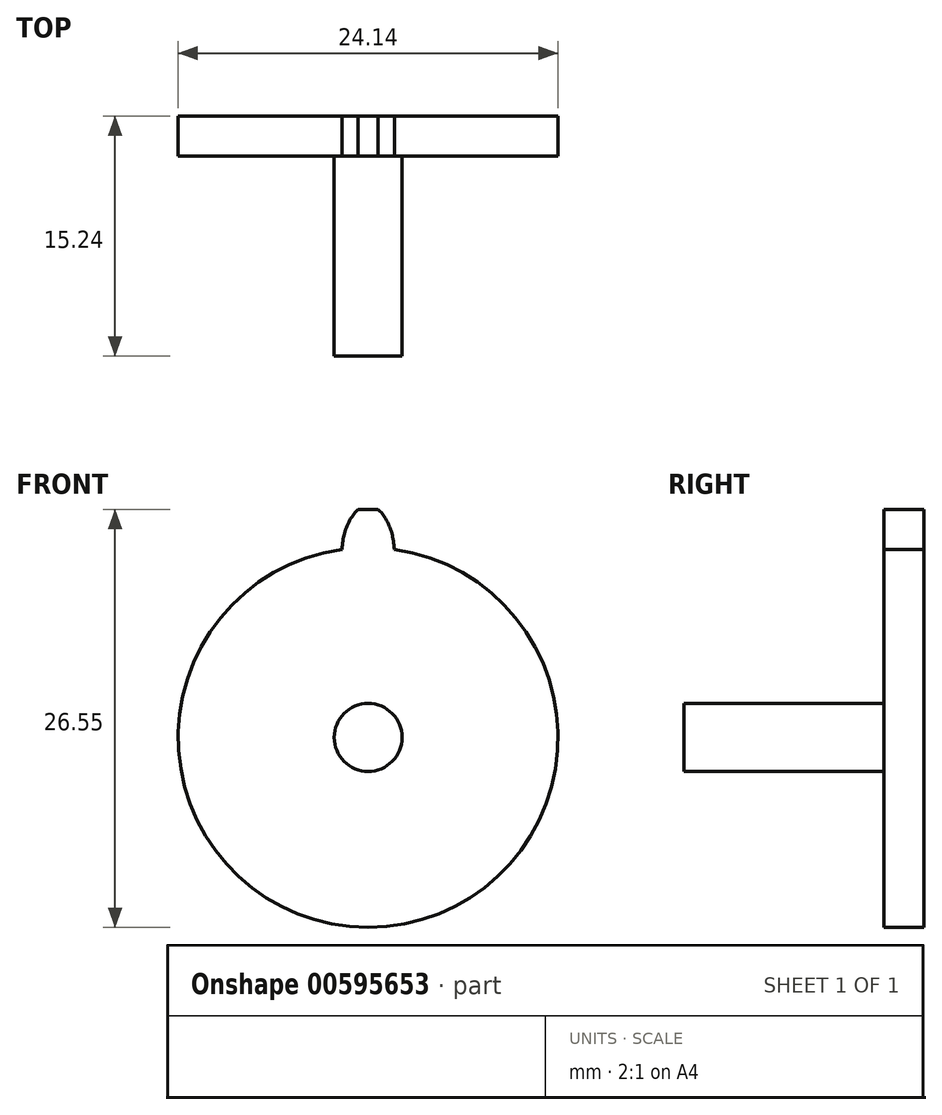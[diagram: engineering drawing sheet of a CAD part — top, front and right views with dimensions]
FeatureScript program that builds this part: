
annotation { "Feature Type Name" : "Feature", "Feature Type Description" : "" }
export const myFeature = defineFeature(function(context is Context, id is Id, definition is map)
    precondition{}
    {
        {
            var Q0;
            Q0=qCreatedBy(makeId("Front.planeOp"),FACE);
            var sketch = newSketch(context, id + "F0", { "sketchPlane" : qUnion([Q0])});
            skCircle(sketch, "E0", {"center": v(0, 0) * mm, "radius": 12.07 * mm});
            skLineSegment(sketch, "E1", {"start": v(-0.64, 14.48) * mm, "end": v(0.64, 14.48) * mm});
            skFitSpline(sketch, "E2", {"points": [v(-1.67, 11.95) * mm, v(-1.33, 13.46) * mm, v(-0.63, 14.48) * mm], "startDerivative": vector(0.3, 3.1) * mm, "endDerivative": vector(1.45, 1) * mm});
            skLineSegment(sketch, "E3", {"start": v(0, 0) * mm, "end": v(0, 0) * mm});
            skLineSegment(sketch, "E4", {"start": v(0, 0) * mm, "end": v(0, 14.48) * mm, "construction": true});
            skFitSpline(sketch, "E5.MirrorCS", {"points": [v(1.67, 11.95) * mm, v(1.33, 13.46) * mm, v(0.63, 14.48) * mm], "startDerivative": vector(-0.3, 3.1) * mm, "endDerivative": vector(-1.45, 1) * mm});
            skSolve(sketch);
        }
        {
            var Q0;
            {var subQ0=sQuery(id+"F0.wireOp",EDGE,"E0");var subQ1=makeQuery(id+"F0.imprint","INTERSECT",VERTEX,{"derivedFrom":[subQ0,sQuery(id+"F0.wireOp",EDGE,"E2")]});Q0=makeQuery(id+"F0.imprint","IMPRINT",FACE,{"disambiguationData":[TD([[makeQuery(id+"F0.imprint","IMPRINT",EDGE,{"disambiguationData":[TD([[subQ1,1.0]])],"derivedFrom":subQ0}),1.0]])]});}
            extrude(context, id + "F1", {"entities" : qUnion([Q0]), "depth" : 2.54 * mm, "offsetDistance" : 25.4 * mm});
        }
        {
            var Q0;
            Q0=makeQuery(id+"F0.imprint","IMPRINT",FACE,{"disambiguationData":[TD([[makeQuery(id+"F0.imprint","IMPRINT",EDGE,{"derivedFrom":sQuery(id+"F0.wireOp",EDGE,"E1")}),-1.0]])]});
            var Q1;
            Q1=makeQuery(id+"F1.opExtrude","CAP_FACE",FACE,{"disambiguationData":[OSD([sQuery(id+"F0.wireOp",EDGE,"E0")])],"isStart":false});
            extrude(context, id + "F2", {"entities" : qUnion([Q0]), "operationType" : NewBodyOperationType.ADD, "endBound" : BoundingType.UP_TO_SURFACE, "depth" : 25.4 * mm, "endBoundEntityFace" : qUnion([Q1]), "offsetDistance" : 25.4 * mm});
        }
        {
            var Q0;
            {var subQ0=sQuery(id+"F0.wireOp",EDGE,"E0");Q0=makeQuery(id+"FnFVmL9Oh5nvcq0_1.4.F2.boolean.opBoolean","MERGE",FACE,{"derivedFrom":[makeQuery(id+"FnFVmL9Oh5nvcq0_1.3.F2.boolean.opBoolean","MERGE",FACE,{"derivedFrom":[makeQuery(id+"FnFVmL9Oh5nvcq0_1.2.F2.boolean.opBoolean","MERGE",FACE,{"derivedFrom":[makeQuery(id+"FnFVmL9Oh5nvcq0_1.1.F2.boolean.opBoolean","MERGE",FACE,{"derivedFrom":[makeQuery(id+"F2.boolean.opBoolean","MERGE",FACE,{"derivedFrom":[makeQuery(id+"F1.opExtrude","CAP_FACE",FACE,{"disambiguationData":[OSD([subQ0])],"isStart":false}),makeQuery(id+"F2.opExtrude","CAP_FACE",FACE,{"disambiguationData":[OSD([subQ0])],"isStart":false})]}),makeQuery(id+"FnFVmL9Oh5nvcq0_1.1.F2.opExtrude","CAP_FACE",FACE,{"disambiguationData":[OSD([subQ0])],"isStart":false})]}),makeQuery(id+"FnFVmL9Oh5nvcq0_1.2.F2.opExtrude","CAP_FACE",FACE,{"disambiguationData":[OSD([subQ0])],"isStart":false})]}),makeQuery(id+"FnFVmL9Oh5nvcq0_1.3.F2.opExtrude","CAP_FACE",FACE,{"disambiguationData":[OSD([subQ0])],"isStart":false})]}),makeQuery(id+"FnFVmL9Oh5nvcq0_1.4.F2.opExtrude","CAP_FACE",FACE,{"disambiguationData":[OSD([subQ0])],"isStart":false})]});}
            var sketch = newSketch(context, id + "F3", { "sketchPlane" : qUnion([Q0])});
            skCircle(sketch, "E6", {"center": v(0, 0) * mm, "radius": 2.16 * mm});
            skSolve(sketch);
        }
        {
            var Q0;
            Q0=makeQuery(id+"F3.imprint","IMPRINT",FACE,{"disambiguationData":[TD([[makeQuery(id+"F3.imprint","IMPRINT",EDGE,{"derivedFrom":sQuery(id+"F3.wireOp",EDGE,"E6")}),1.0]])]});
            extrude(context, id + "F4", {"entities" : qUnion([Q0]), "operationType" : NewBodyOperationType.ADD, "depth" : 12.7 * mm, "offsetDistance" : 25.4 * mm});
        }
    });
